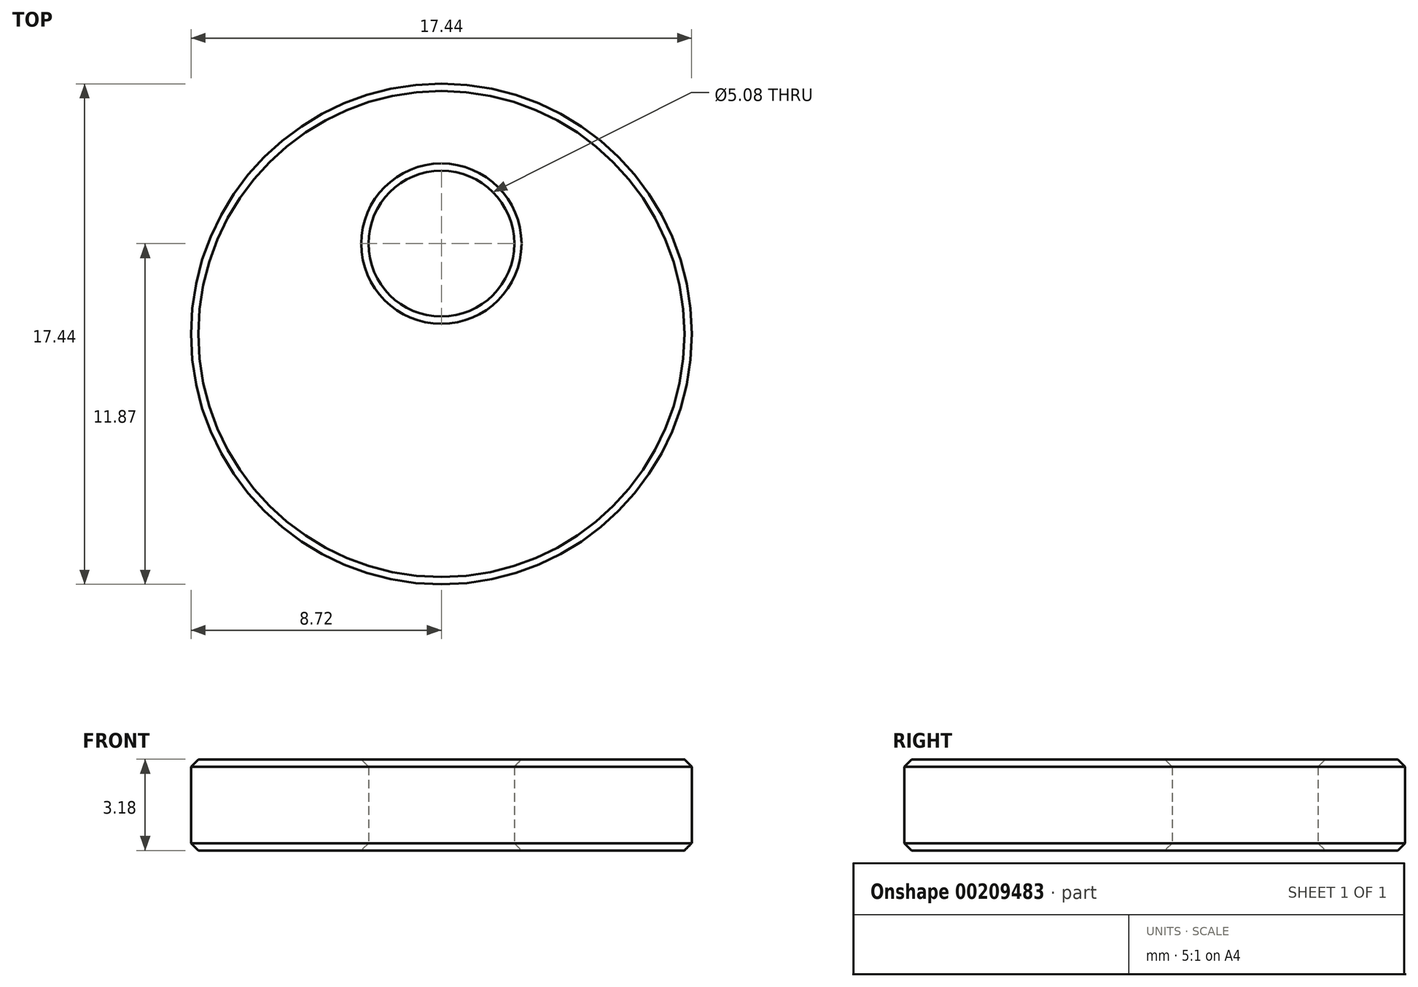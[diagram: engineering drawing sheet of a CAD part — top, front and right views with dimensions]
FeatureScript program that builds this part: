
annotation { "Feature Type Name" : "Feature", "Feature Type Description" : "" }
export const myFeature = defineFeature(function(context is Context, id is Id, definition is map)
    precondition{}
    {
        {
            var Q0;
            Q0=qCreatedBy(makeId("Top.planeOp"),FACE);
            var sketch = newSketch(context, id + "F0", { "sketchPlane" : qUnion([Q0])});
            skCircle(sketch, "E0", {"center": v(0, 0) * mm, "radius": 8.72 * mm});
            skCircle(sketch, "E1", {"center": v(0, 3.15) * mm, "radius": 2.54 * mm});
            skSolve(sketch);
        }
        {
            var Q0;
            Q0 = qSketchRegion(id + "F0", true);
            extrude(context, id + "F1", {"entities" : qUnion([Q0]), "depth" : 3.17 * mm});
        }
        {
            var Q0;
            Q0=makeQuery(id+"F1.opExtrude","CAP_EDGE",EDGE,{"disambiguationData":[OSD([sQuery(id+"F0.wireOp",EDGE,"E0")])],"isStart":false});
            var Q1;
            Q1=makeQuery(id+"F1.opExtrude","CAP_EDGE",EDGE,{"disambiguationData":[OSD([sQuery(id+"F0.wireOp",EDGE,"E0")])],"isStart":true});
            var Q2;
            Q2=makeQuery(id+"F1.opExtrude","CAP_EDGE",EDGE,{"disambiguationData":[OSD([sQuery(id+"F0.wireOp",EDGE,"E1")])],"isStart":false});
            var Q3;
            Q3=makeQuery(id+"F1.opExtrude","CAP_EDGE",EDGE,{"disambiguationData":[OSD([sQuery(id+"F0.wireOp",EDGE,"E1")])],"isStart":true});
            chamfer(context, id + "F2", {"entities" : qUnion([Q0, Q1, Q2, Q3]), "width" : 0.25 * mm, "tangentPropagation" : true});
        }
    });
